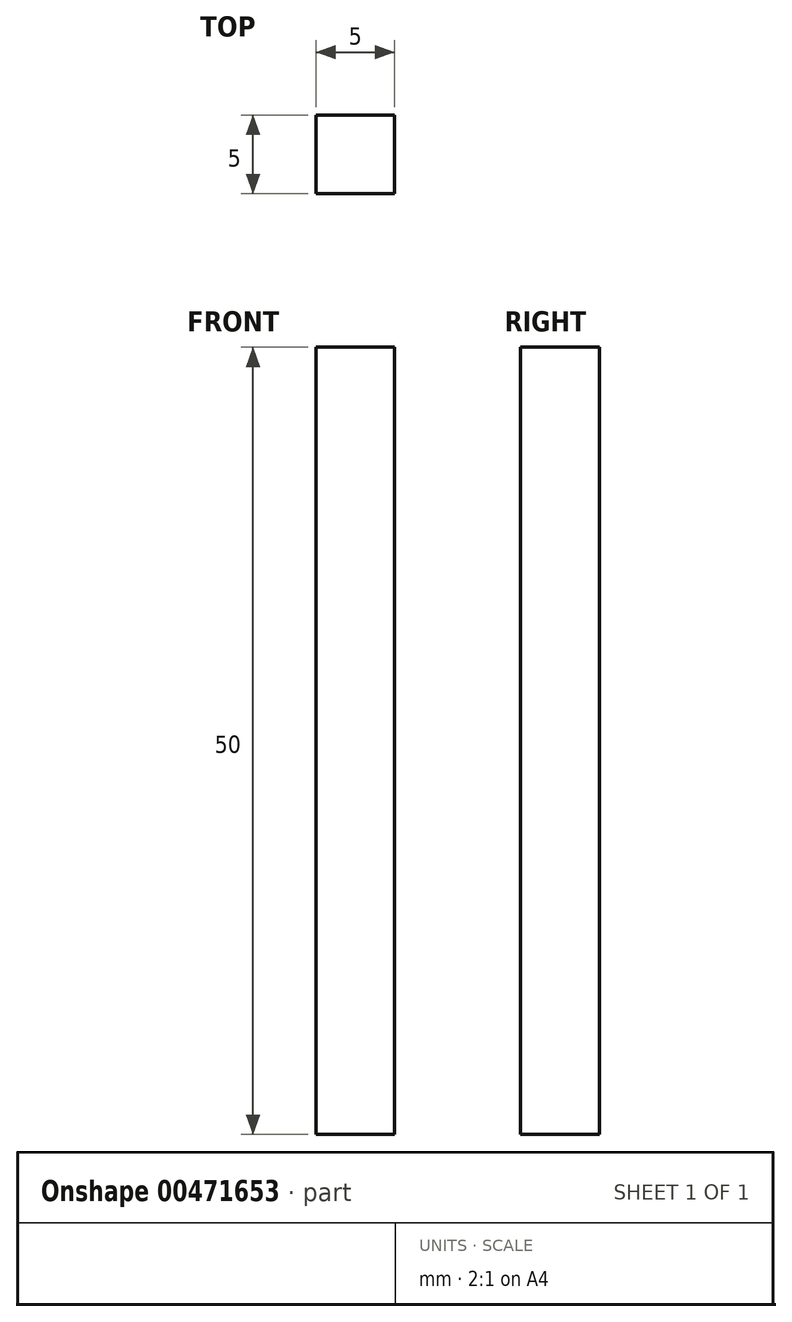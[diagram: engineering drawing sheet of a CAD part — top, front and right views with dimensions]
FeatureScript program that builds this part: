
annotation { "Feature Type Name" : "Feature", "Feature Type Description" : "" }
export const myFeature = defineFeature(function(context is Context, id is Id, definition is map)
    precondition{}
    {
        {
            var Q0;
            Q0=qCreatedBy(makeId("Front.planeOp"),FACE);
            var sketch = newSketch(context, id + "F0", { "sketchPlane" : qUnion([Q0])});
            skLineSegment(sketch, "E0.bottom", {"start": v(-24.46, 12.41) * mm, "end": v(-19.46, 12.41) * mm});
            skLineSegment(sketch, "E0.top", {"start": v(-24.46, -37.59) * mm, "end": v(-19.46, -37.59) * mm});
            skLineSegment(sketch, "E0.left", {"start": v(-24.46, 12.41) * mm, "end": v(-24.46, -37.59) * mm});
            skLineSegment(sketch, "E0.right", {"start": v(-19.46, 12.41) * mm, "end": v(-19.46, -37.59) * mm});
            skSolve(sketch);
        }
        {
            var Q0;
            Q0 = qSketchRegion(id + "F0", true);
            extrude(context, id + "F1", {"entities" : qUnion([Q0]), "depth" : 5 * mm});
        }
    });
